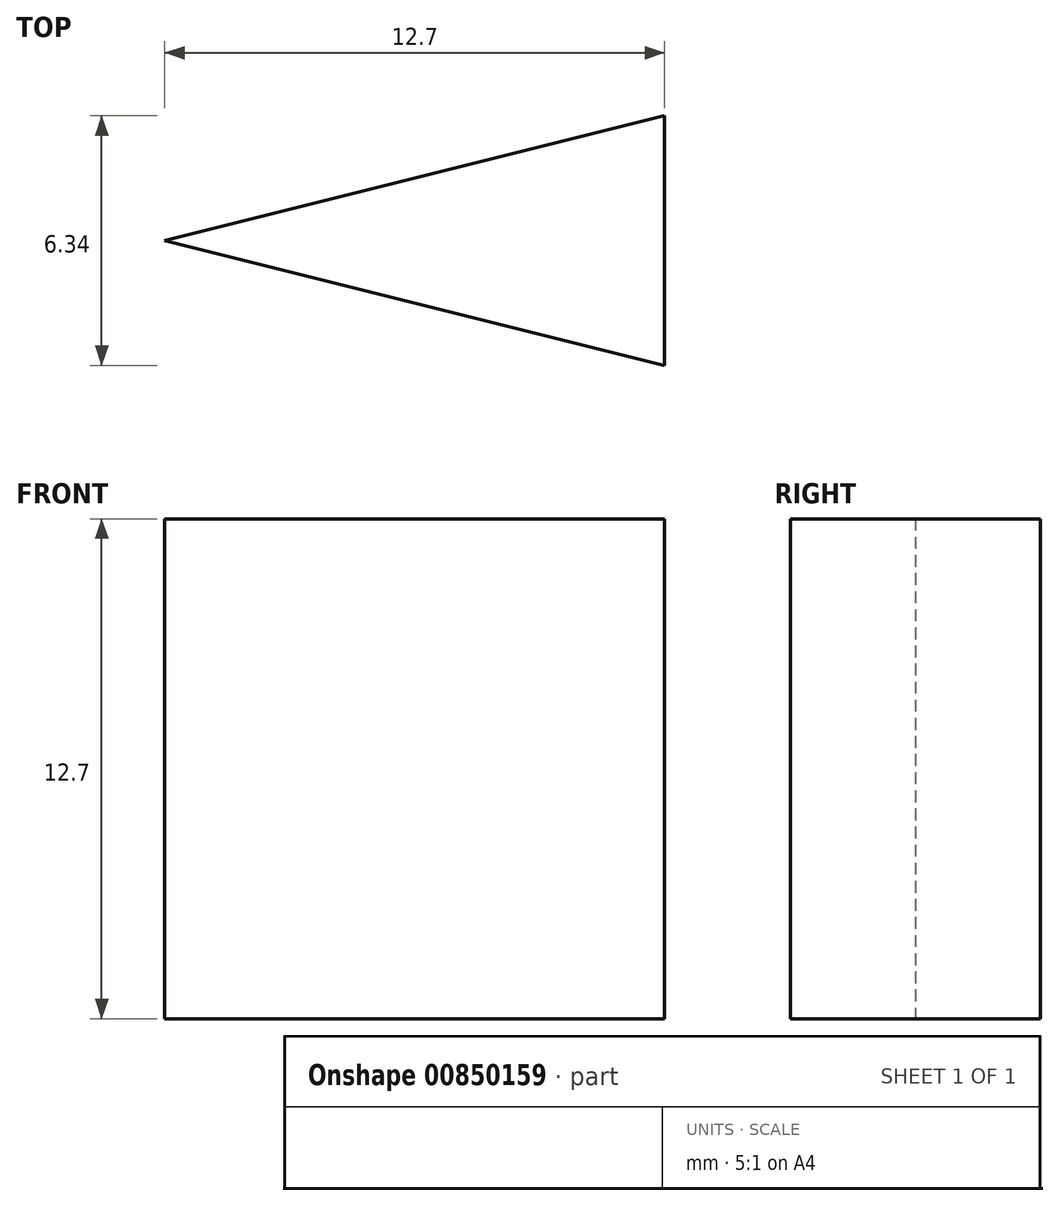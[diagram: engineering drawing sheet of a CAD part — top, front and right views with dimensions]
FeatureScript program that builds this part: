
annotation { "Feature Type Name" : "Feature", "Feature Type Description" : "" }
export const myFeature = defineFeature(function(context is Context, id is Id, definition is map)
    precondition{}
    {
        {
            var Q0;
            Q0=qCreatedBy(makeId("Top.planeOp"),FACE);
            var sketch = newSketch(context, id + "F0", { "sketchPlane" : qUnion([Q0])});
            skLineSegment(sketch, "E0", {"start": v(-12.7, 0) * mm, "end": v(0, 3.17) * mm});
            skLineSegment(sketch, "E1", {"start": v(0, 3.18) * mm, "end": v(12.7, 0) * mm});
            skLineSegment(sketch, "E2", {"start": v(12.7, 0) * mm, "end": v(0, -3.17) * mm});
            skLineSegment(sketch, "E3", {"start": v(0, -3.17) * mm, "end": v(-12.7, 0) * mm});
            skLineSegment(sketch, "E4", {"start": v(0, -3.17) * mm, "end": v(0, 3.17) * mm});
            skSolve(sketch);
        }
        {
            var Q0;
            Q0=makeQuery(id+"F0.imprint","IMPRINT",FACE,{"disambiguationData":[TD([[makeQuery(id+"F0.imprint","IMPRINT",EDGE,{"derivedFrom":sQuery(id+"F0.wireOp",EDGE,"E0")}),-1.0]])]});
            extrude(context, id + "F1", {"entities" : qUnion([Q0]), "depth" : 12.7 * mm, "offsetDistance" : 25.4 * mm});
        }
    });
